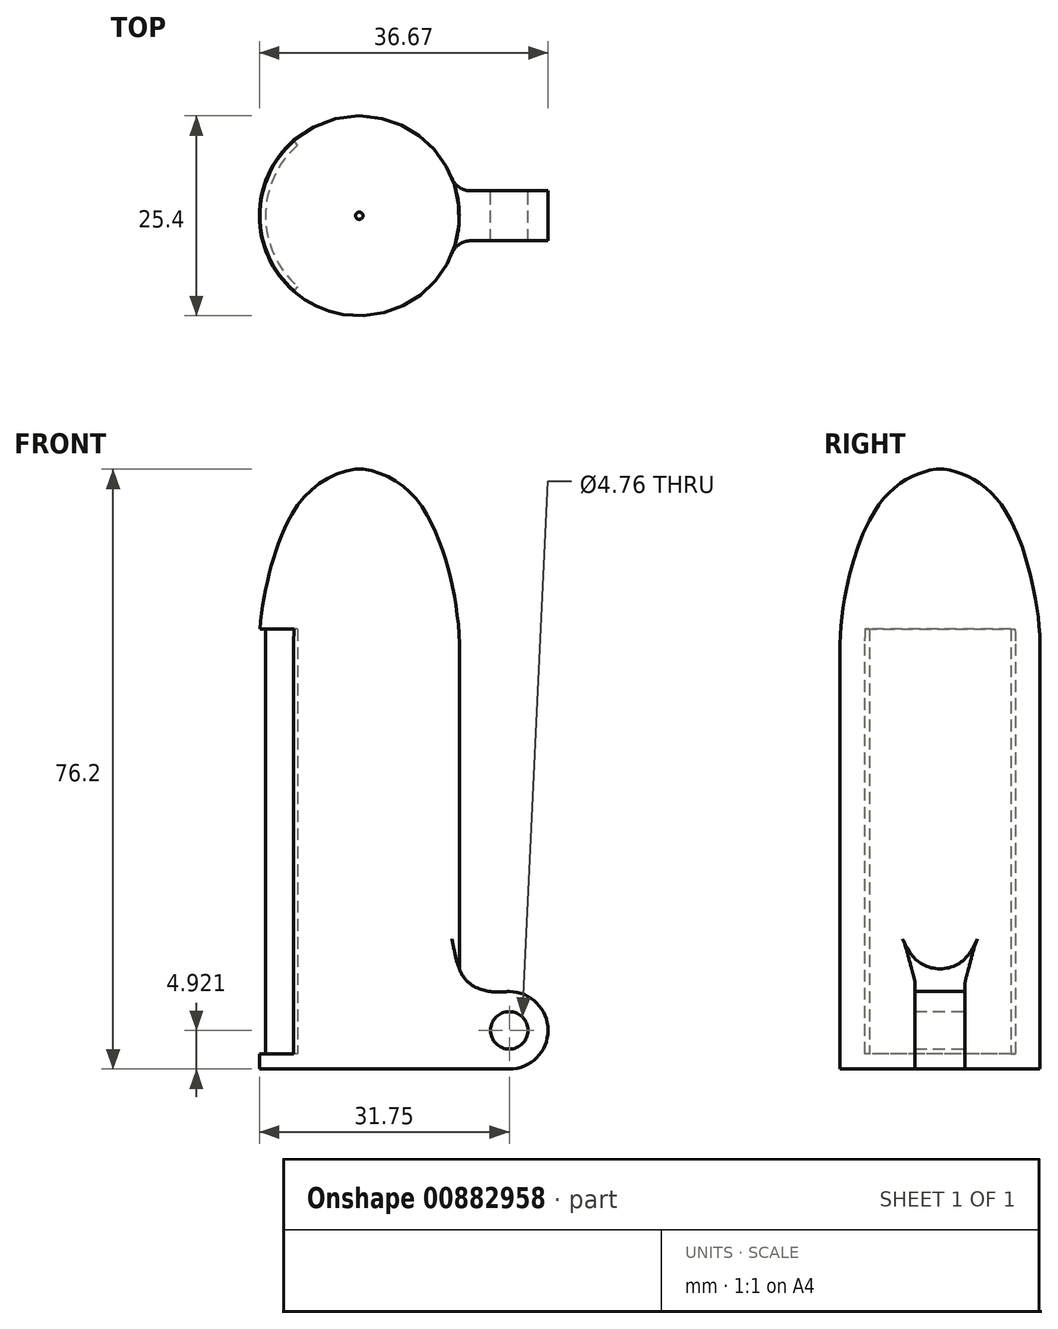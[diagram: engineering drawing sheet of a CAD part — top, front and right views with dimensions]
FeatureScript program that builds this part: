
annotation { "Feature Type Name" : "Feature", "Feature Type Description" : "" }
export const myFeature = defineFeature(function(context is Context, id is Id, definition is map)
    precondition{}
    {
        {
            var Q0;
            Q0=qCreatedBy(makeId("Front.planeOp"),FACE);
            var sketch = newSketch(context, id + "F0", { "sketchPlane" : qUnion([Q0])});
            skLineSegment(sketch, "E0.bottom", {"start": v(0, 0) * mm, "end": v(12.7, 0) * mm});
            skLineSegment(sketch, "E0.top", {"start": v(0, 76.2) * mm, "end": v(12.7, 76.2) * mm});
            skLineSegment(sketch, "E0.left", {"start": v(0, 0) * mm, "end": v(0, 76.2) * mm});
            skLineSegment(sketch, "E0.right", {"start": v(12.7, 0) * mm, "end": v(12.7, 76.2) * mm});
            skFitSpline(sketch, "E1", {"points": [v(0, 76.2) * mm, v(6.9, 72.8) * mm, v(12.7, 54.03) * mm], "startDerivative": vector(7.47, 0.84) * mm, "endDerivative": vector(0, -21.96) * mm});
            skSolve(sketch);
        }
        {
            var Q0;
            {var subQ1=sQuery(id+"F0.wireOp",EDGE,"E0.bottom");Q0=makeQuery(id+"F0.imprint","IMPRINT",FACE,{"disambiguationData":[TD([[makeQuery(id+"F0.imprint","IMPRINT",EDGE,{"derivedFrom":subQ1}),1.0]])]});}
            var Q1;
            Q1=sQuery(id+"F0.wireOp",EDGE,"E0.left");
            revolve(context, id + "F1", {"surfaceOperationType" : NewSurfaceOperationType.NEW, "entities" : qUnion([Q0]), "axis" : qUnion([Q1]), "revolveType" : RevolveType.FULL});
        }
        {
            var Q0;
            Q0=qCreatedBy(makeId("Front.planeOp"),FACE);
            var sketch = newSketch(context, id + "F2", { "sketchPlane" : qUnion([Q0])});
            skCircle(sketch, "E2", {"center": v(19.05, 4.92) * mm, "radius": 2.38 * mm});
            skCircle(sketch, "E3.0", {"center": v(19.05, 4.92) * mm, "radius": 4.92 * mm});
            skLineSegment(sketch, "E4", {"start": v(12.7, 54.23) * mm, "end": v(12.7, 0) * mm});
            skLineSegment(sketch, "E5", {"start": v(19.05, 0) * mm, "end": v(11.52, 0) * mm});
            skLineSegment(sketch, "E6", {"start": v(11.52, 0) * mm, "end": v(11.52, 11.14) * mm});
            skFitSpline(sketch, "E7", {"points": [v(19.05, 9.84) * mm, v(16.6, 9.86) * mm, v(13.27, 11.67) * mm, v(11.52, 17.64) * mm], "startDerivative": vector(-8.43, -0.01) * mm, "endDerivative": vector(-3.56, 13.66) * mm});
            skLineSegment(sketch, "E8", {"start": v(11.52, 17.64) * mm, "end": v(11.52, 11.14) * mm});
            skSolve(sketch);
        }
        {
            var Q0;
            Q0 = qSketchRegion(id + "F2", true);
            extrude(context, id + "F3", {"entities" : qUnion([Q0]), "operationType" : NewBodyOperationType.ADD, "depth" : 3.17 * mm, "offsetDistance" : 25.4 * mm, "hasSecondDirection" : true, "secondDirectionOppositeDirection" : true, "secondDirectionDepth" : 3.17 * mm});
        }
        {
            var Q0;
            Q0=makeQuery(id+"F3.boolean.opBoolean","INTERSECT",EDGE,{"derivedFrom":[makeQuery(id+"F1.opRevolve","SWEPT_FACE",FACE,{"disambiguationData":[OSD([sQuery(id+"F0.wireOp",EDGE,"E0.right")])]}),makeQuery(id+"F3.opExtrude","CAP_FACE",FACE,{"disambiguationData":[OSD([sQuery(id+"F2.wireOp",EDGE,"E2"),sQuery(id+"F2.wireOp",EDGE,"E3.0"),sQuery(id+"F2.wireOp",EDGE,"E5"),sQuery(id+"F2.wireOp",EDGE,"E6"),sQuery(id+"F2.wireOp",EDGE,"E7"),sQuery(id+"F2.wireOp",EDGE,"E8")])],"isStart":true})]});
            var Q1;
            Q1=makeQuery(id+"F3.boolean.opBoolean","INTERSECT",EDGE,{"derivedFrom":[makeQuery(id+"F1.opRevolve","SWEPT_FACE",FACE,{"disambiguationData":[OSD([sQuery(id+"F0.wireOp",EDGE,"E0.right")])]}),makeQuery(id+"F3.opExtrude","CAP_FACE",FACE,{"disambiguationData":[OSD([sQuery(id+"F2.wireOp",EDGE,"E2"),sQuery(id+"F2.wireOp",EDGE,"E3.0"),sQuery(id+"F2.wireOp",EDGE,"E5"),sQuery(id+"F2.wireOp",EDGE,"E6"),sQuery(id+"F2.wireOp",EDGE,"E7"),sQuery(id+"F2.wireOp",EDGE,"E8")])],"isStart":false})]});
            fillet(context, id + "F4", {"entities" : qUnion([Q0, Q1]), "radius" : 2.54 * mm, "tangentPropagation" : true, "allowEdgeOverflow" : false});
        }
        {
            var Q0;
            Q0=qCreatedBy(makeId("Front.planeOp"),FACE);
            var sketch = newSketch(context, id + "F5", { "sketchPlane" : qUnion([Q0])});
            skLineSegment(sketch, "E9.bottom", {"start": v(-11.9, 55.88) * mm, "end": v(-19.16, 55.88) * mm});
            skLineSegment(sketch, "E9.top", {"start": v(-11.9, 1.9) * mm, "end": v(-19.16, 1.9) * mm});
            skLineSegment(sketch, "E9.left", {"start": v(-11.9, 55.88) * mm, "end": v(-11.9, 1.9) * mm});
            skLineSegment(sketch, "E9.right", {"start": v(-19.16, 55.88) * mm, "end": v(-19.16, 1.9) * mm});
            skLineSegment(sketch, "E10", {"start": v(-12.7, 0) * mm, "end": v(-12.7, 54.03) * mm});
            skLineSegment(sketch, "E11", {"start": v(0, 0) * mm, "end": v(0, 75.88) * mm});
            skSolve(sketch);
        }
        {
            var Q0;
            Q0=makeQuery(id+"F5.imprint","IMPRINT",FACE,{"disambiguationData":[TD([[makeQuery(id+"F5.imprint","IMPRINT",EDGE,{"derivedFrom":sQuery(id+"F5.wireOp",EDGE,"E9.bottom")}),1.0]])]});
            var Q1;
            Q1=sQuery(id+"F5.wireOp",EDGE,"E11");
            revolve(context, id + "F6", {"operationType" : NewBodyOperationType.REMOVE, "surfaceOperationType" : NewSurfaceOperationType.NEW, "entities" : qUnion([Q0]), "axis" : qUnion([Q1]), "revolveType" : RevolveType.SYMMETRIC, "oppositeDirection" : true, "angle" : 98 * degree});
        }
    });
